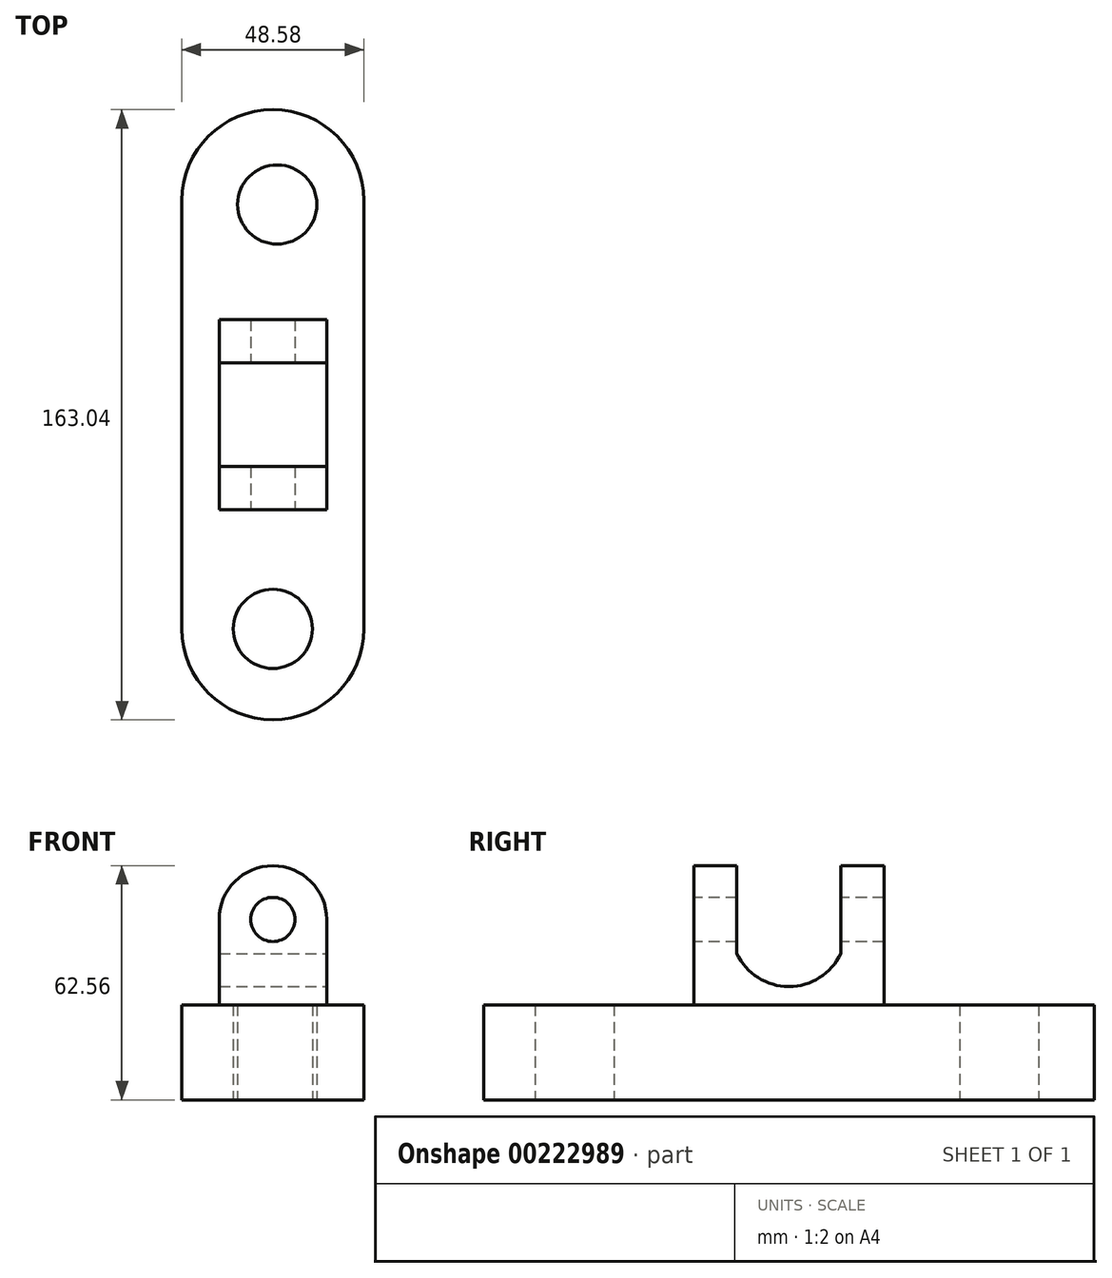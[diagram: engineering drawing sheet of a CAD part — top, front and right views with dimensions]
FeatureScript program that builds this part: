
annotation { "Feature Type Name" : "Feature", "Feature Type Description" : "" }
export const myFeature = defineFeature(function(context is Context, id is Id, definition is map)
    precondition{}
    {
        {
            var Q0;
            Q0=qCreatedBy(makeId("Top.planeOp"),FACE);
            var sketch = newSketch(context, id + "F0", { "sketchPlane" : qUnion([Q0])});
            skLineSegment(sketch, "E0.bottom", {"start": v(24.29, 57.23) * mm, "end": v(-24.29, 57.23) * mm});
            skLineSegment(sketch, "E0.top", {"start": v(24.29, -57.23) * mm, "end": v(-24.29, -57.23) * mm});
            skLineSegment(sketch, "E0.left", {"start": v(24.29, 57.23) * mm, "end": v(24.29, -57.23) * mm});
            skLineSegment(sketch, "E0.right", {"start": v(-24.29, 57.23) * mm, "end": v(-24.29, -57.23) * mm});
            skPoint(sketch, "E0.middle", {"position": v(0, 0) * mm});
            skArc(sketch, "E1", {"start": v(-24.29, -57.23) * mm, "mid": v(0, -81.52) * mm, "end": v(24.29, -57.23) * mm});
            skArc(sketch, "E2", {"start": v(24.29, 57.23) * mm, "mid": v(0, 81.52) * mm, "end": v(-24.29, 57.23) * mm});
            skCircle(sketch, "E3", {"center": v(0, -57.23) * mm, "radius": 10.58 * mm});
            skCircle(sketch, "E4", {"center": v(1.16, 56.16) * mm, "radius": 10.58 * mm});
            skSolve(sketch);
        }
        {
            var Q0;
            {var subQ5=sQuery(id+"F0.wireOp",EDGE,"E0.left");Q0=makeQuery(id+"F0.imprint","IMPRINT",FACE,{"disambiguationData":[TD([[makeQuery(id+"F0.imprint","IMPRINT",EDGE,{"derivedFrom":subQ5}),-1.0]])]});}
            var Q1;
            {var subQ0=sQuery(id+"F0.wireOp",EDGE,"E1");Q1=makeQuery(id+"F0.imprint","IMPRINT",FACE,{"disambiguationData":[TD([[makeQuery(id+"F0.imprint","IMPRINT",EDGE,{"derivedFrom":subQ0}),1.0]])]});}
            var Q2;
            {var subQ0=sQuery(id+"F0.wireOp",EDGE,"E2");Q2=makeQuery(id+"F0.imprint","IMPRINT",FACE,{"disambiguationData":[TD([[makeQuery(id+"F0.imprint","IMPRINT",EDGE,{"derivedFrom":subQ0}),1.0]])]});}
            extrude(context, id + "F1", {"entities" : qUnion([Q0, Q1, Q2]), "depth" : 25.4 * mm});
        }
        {
            var Q0;
            Q0=qCreatedBy(makeId("Front.planeOp"),FACE);
            var sketch = newSketch(context, id + "F2", { "sketchPlane" : qUnion([Q0])});
            skLineSegment(sketch, "E5.bottom", {"start": v(14.35, 48.2) * mm, "end": v(-14.35, 48.2) * mm});
            skLineSegment(sketch, "E5.top", {"start": v(14.35, 3.55) * mm, "end": v(-14.35, 3.55) * mm});
            skLineSegment(sketch, "E5.left", {"start": v(14.35, 48.2) * mm, "end": v(14.35, 3.55) * mm});
            skLineSegment(sketch, "E5.right", {"start": v(-14.35, 48.2) * mm, "end": v(-14.35, 3.55) * mm});
            skPoint(sketch, "E5.middle", {"position": v(0, 25.88) * mm});
            skArc(sketch, "E6", {"start": v(14.35, 48.2) * mm, "mid": v(0, 62.56) * mm, "end": v(-14.35, 48.2) * mm});
            skSolve(sketch);
        }
        {
            var Q0;
            Q0=makeQuery(id+"F2.imprint","IMPRINT",FACE,{"disambiguationData":[TD([[makeQuery(id+"F2.imprint","IMPRINT",EDGE,{"derivedFrom":sQuery(id+"F2.wireOp",EDGE,"E5.bottom")}),1.0]])]});
            var Q1;
            Q1=makeQuery(id+"F2.imprint","IMPRINT",FACE,{"disambiguationData":[TD([[makeQuery(id+"F2.imprint","IMPRINT",EDGE,{"derivedFrom":sQuery(id+"F2.wireOp",EDGE,"E5.bottom")}),-1.0]])]});
            extrude(context, id + "F3", {"entities" : qUnion([Q0, Q1]), "operationType" : NewBodyOperationType.ADD, "depth" : 25.4 * mm});
        }
        {
            var Q0;
            Q0=makeQuery(id+"F3.opExtrude","CAP_FACE",FACE,{"disambiguationData":[OSD([sQuery(id+"F2.wireOp",EDGE,"E5.top"),sQuery(id+"F2.wireOp",EDGE,"E5.left"),sQuery(id+"F2.wireOp",EDGE,"E5.right"),sQuery(id+"F2.wireOp",EDGE,"E6")])],"isStart":true});
            extrude(context, id + "F4", {"entities" : qUnion([Q0]), "operationType" : NewBodyOperationType.ADD, "depth" : 25.4 * mm});
        }
        {
            var Q0;
            Q0=makeQuery(id+"F3.opExtrude","CAP_FACE",FACE,{"disambiguationData":[OSD([sQuery(id+"F2.wireOp",EDGE,"E5.top"),sQuery(id+"F2.wireOp",EDGE,"E5.left"),sQuery(id+"F2.wireOp",EDGE,"E5.right"),sQuery(id+"F2.wireOp",EDGE,"E6")])],"isStart":false});
            var sketch = newSketch(context, id + "F5", { "sketchPlane" : qUnion([Q0])});
            skCircle(sketch, "E7", {"center": v(0, 48.2) * mm, "radius": 5.9 * mm});
            skSolve(sketch);
        }
        {
            var Q0;
            Q0 = qSketchRegion(id + "F5", true);
            extrude(context, id + "F6", {"entities" : qUnion([Q0]), "operationType" : NewBodyOperationType.REMOVE, "endBound" : BoundingType.THROUGH_ALL, "oppositeDirection" : true, "depth" : 25.4 * mm});
        }
        {
            var Q0;
            {var subQ0=sQuery(id+"F2.wireOp",EDGE,"E5.left");Q0=makeQuery(id+"F4.boolean.opBoolean","MERGE",FACE,{"derivedFrom":[makeQuery(id+"F3.opExtrude","SWEPT_FACE",FACE,{"disambiguationData":[OSD([subQ0])]}),makeQuery(id+"F4.opExtrude","SWEPT_FACE",FACE,{"disambiguationData":[OSD([subQ0])]})]});}
            var sketch = newSketch(context, id + "F7", { "sketchPlane" : qUnion([Q0])});
            skLineSegment(sketch, "E8", {"start": v(-25.4, 62.56) * mm, "end": v(25.4, 62.56) * mm});
            skLineSegment(sketch, "E9", {"start": v(-13.87, 62.56) * mm, "end": v(-13.87, 39.1) * mm});
            skLineSegment(sketch, "E10", {"start": v(-13.87, 39.1) * mm, "end": v(13.87, 39.1) * mm});
            skLineSegment(sketch, "E11", {"start": v(13.87, 39.1) * mm, "end": v(13.87, 62.56) * mm});
            skArc(sketch, "E12", {"start": v(-13.87, 39.1) * mm, "mid": v(0, 30.26) * mm, "end": v(13.87, 39.1) * mm});
            skSolve(sketch);
        }
        {
            var Q0;
            Q0=makeQuery(id+"F7.imprint","IMPRINT",FACE,{"disambiguationData":[TD([[makeQuery(id+"F7.imprint","IMPRINT",EDGE,{"derivedFrom":sQuery(id+"F7.wireOp",EDGE,"E10")}),-1.0]])]});
            var Q1;
            {var subQ1=sQuery(id+"F7.wireOp",EDGE,"E10");Q1=makeQuery(id+"F7.imprint","IMPRINT",FACE,{"disambiguationData":[TD([[makeQuery(id+"F7.imprint","IMPRINT",EDGE,{"derivedFrom":subQ1}),1.0]])]});}
            var Q2;
            {var subQ0=sQuery(id+"F7.wireOp",EDGE,"E9");var subQ1=sQuery(id+"F7.wireOp",EDGE,"E8");var subQ2=makeQuery(id+"F7.imprint","INTERSECT",VERTEX,{"derivedFrom":[subQ1,subQ0]});Q2=makeQuery(id+"F7.imprint","IMPRINT",FACE,{"disambiguationData":[TD([[makeQuery(id+"F7.imprint","IMPRINT",EDGE,{"disambiguationData":[TD([[subQ2,-1.0]])],"derivedFrom":subQ1}),-1.0]])]});}
            extrude(context, id + "F8", {"entities" : qUnion([Q0, Q1, Q2]), "operationType" : NewBodyOperationType.REMOVE, "endBound" : BoundingType.THROUGH_ALL, "oppositeDirection" : true, "depth" : 25.4 * mm});
        }
    });
